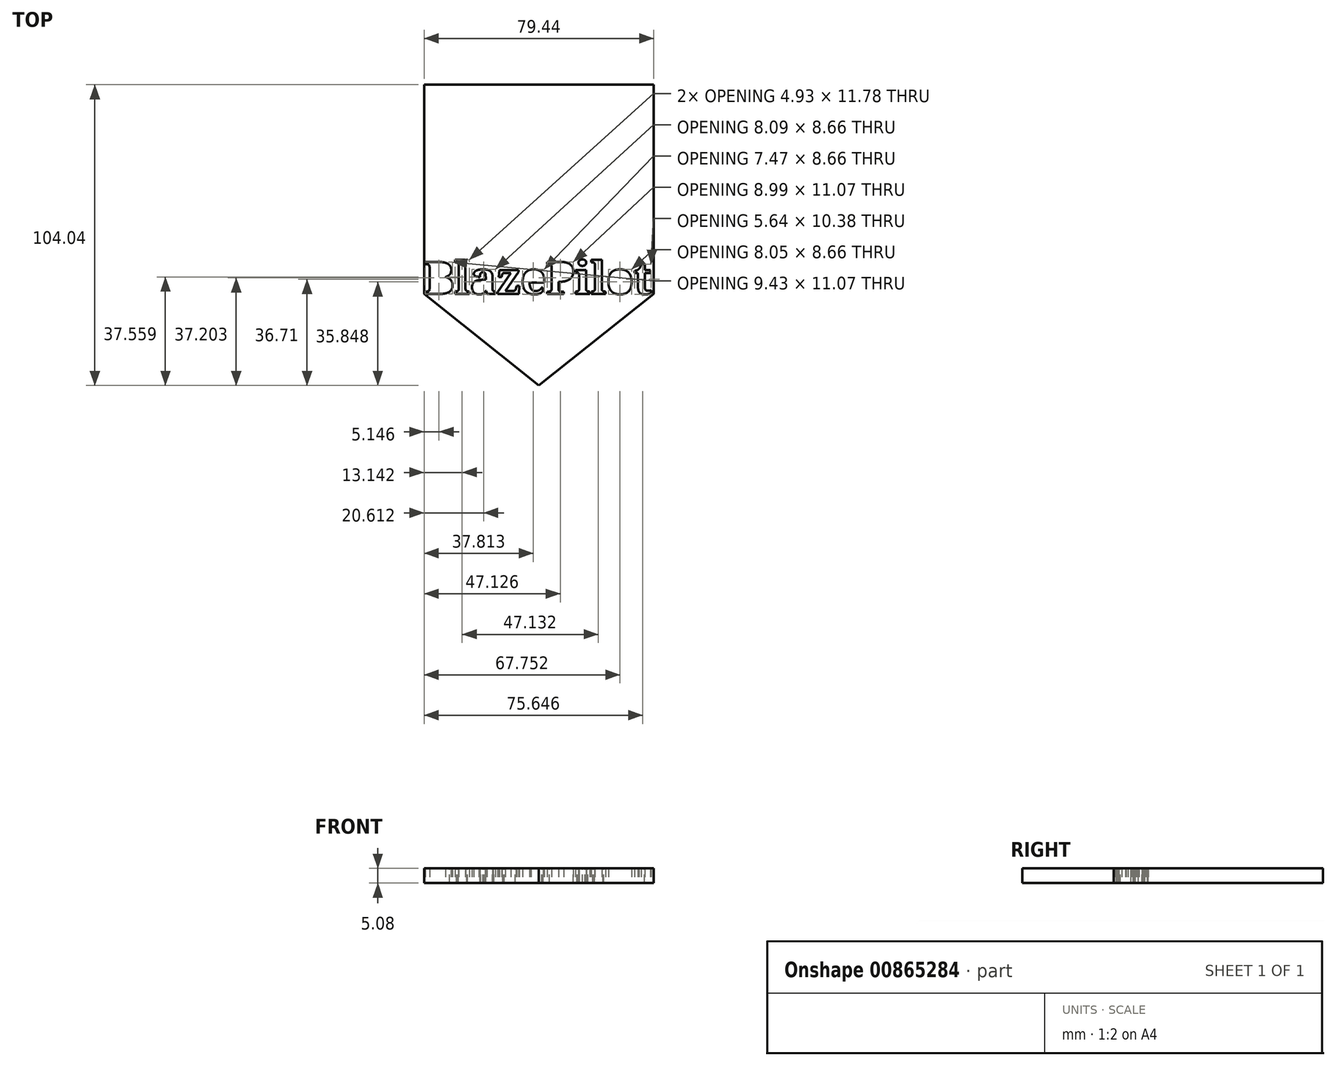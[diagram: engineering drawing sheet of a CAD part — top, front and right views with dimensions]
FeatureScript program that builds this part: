
annotation { "Feature Type Name" : "Feature", "Feature Type Description" : "" }
export const myFeature = defineFeature(function(context is Context, id is Id, definition is map)
    precondition{}
    {
        {
            var Q0;
            Q0=qCreatedBy(makeId("Top.planeOp"),FACE);
            var sketch = newSketch(context, id + "F0", { "sketchPlane" : qUnion([Q0])});
            skLineSegment(sketch, "E0", {"start": v(0, -55.27) * mm, "end": v(-39.72, -23.6) * mm});
            skLineSegment(sketch, "E1", {"start": v(0, -55.27) * mm, "end": v(39.72, -23.6) * mm});
            skLineSegment(sketch, "E2", {"start": v(-39.72, -23.6) * mm, "end": v(-39.72, 48.77) * mm});
            skLineSegment(sketch, "E3", {"start": v(39.72, -23.6) * mm, "end": v(39.72, 48.77) * mm});
            skLineSegment(sketch, "E4", {"start": v(-39.72, 48.77) * mm, "end": v(39.72, 48.77) * mm});
            skText(sketch, "E5", { "text": "BlazePilot", "fontName": "NotoSerif-Bold.ttf"});
            skLineSegment(sketch, "E6", {"start": v(-36.16, -10.08) * mm, "end": v(21.17, -10.08) * mm});
            const initialGuessF0  = {"E5": [-0.03972, -0.0236, 1, 0, 0.01116]};
            skSetInitialGuess(sketch, initialGuessF0);
            skSolve(sketch);
        }
        {
            var Q0;
            Q0 = qSketchRegion(id + "F0", true);
            extrude(context, id + "F1", {"entities" : qUnion([Q0]), "depth" : 2.54 * mm, "offsetDistance" : 25.4 * mm});
        }
        {
            var Q0;
            Q0 = qSketchRegion(id + "F0", true);
            var Q1;
            Q1=makeQuery(id+"F1.opExtrude","CAP_FACE",FACE,{"disambiguationData":[OSD([sQuery(id+"F0.wireOp",EDGE,"E0"),sQuery(id+"F0.wireOp",EDGE,"E1"),sQuery(id+"F0.wireOp",EDGE,"E2"),sQuery(id+"F0.wireOp",EDGE,"E3"),sQuery(id+"F0.wireOp",EDGE,"E4"),sQuery(id+"F0.wireOp",EDGE,"E5.sketch_text.stroke-0"),sQuery(id+"F0.wireOp",EDGE,"E5.sketch_text.stroke-1"),sQuery(id+"F0.wireOp",EDGE,"E5.sketch_text.stroke-2"),sQuery(id+"F0.wireOp",EDGE,"E5.sketch_text.stroke-3"),sQuery(id+"F0.wireOp",EDGE,"E5.sketch_text.stroke-4"),sQuery(id+"F0.wireOp",EDGE,"E5.sketch_text.stroke-5"),sQuery(id+"F0.wireOp",EDGE,"E5.sketch_text.stroke-6"),sQuery(id+"F0.wireOp",EDGE,"E5.sketch_text.stroke-7"),sQuery(id+"F0.wireOp",EDGE,"E5.sketch_text.stroke-8"),sQuery(id+"F0.wireOp",EDGE,"E5.sketch_text.stroke-9"),sQuery(id+"F0.wireOp",EDGE,"E5.sketch_text.stroke-10"),sQuery(id+"F0.wireOp",EDGE,"E5.sketch_text.stroke-11"),sQuery(id+"F0.wireOp",EDGE,"E5.sketch_text.stroke-12"),sQuery(id+"F0.wireOp",EDGE,"E5.sketch_text.stroke-13"),sQuery(id+"F0.wireOp",EDGE,"E5.sketch_text.stroke-14"),sQuery(id+"F0.wireOp",EDGE,"E5.sketch_text.stroke-15"),sQuery(id+"F0.wireOp",EDGE,"E5.sketch_text.stroke-16"),sQuery(id+"F0.wireOp",EDGE,"E5.sketch_text.stroke-17"),sQuery(id+"F0.wireOp",EDGE,"E5.sketch_text.stroke-18"),sQuery(id+"F0.wireOp",EDGE,"E5.sketch_text.stroke-19"),sQuery(id+"F0.wireOp",EDGE,"E5.sketch_text.stroke-20"),sQuery(id+"F0.wireOp",EDGE,"E5.sketch_text.stroke-21"),sQuery(id+"F0.wireOp",EDGE,"E5.sketch_text.stroke-22"),sQuery(id+"F0.wireOp",EDGE,"E5.sketch_text.stroke-23"),sQuery(id+"F0.wireOp",EDGE,"E5.sketch_text.stroke-24"),sQuery(id+"F0.wireOp",EDGE,"E5.sketch_text.stroke-25"),sQuery(id+"F0.wireOp",EDGE,"E5.sketch_text.stroke-26"),sQuery(id+"F0.wireOp",EDGE,"E5.sketch_text.stroke-27"),sQuery(id+"F0.wireOp",EDGE,"E5.sketch_text.stroke-50"),sQuery(id+"F0.wireOp",EDGE,"E5.sketch_text.stroke-51"),sQuery(id+"F0.wireOp",EDGE,"E5.sketch_text.stroke-52"),sQuery(id+"F0.wireOp",EDGE,"E5.sketch_text.stroke-53"),sQuery(id+"F0.wireOp",EDGE,"E5.sketch_text.stroke-54"),sQuery(id+"F0.wireOp",EDGE,"E5.sketch_text.stroke-55"),sQuery(id+"F0.wireOp",EDGE,"E5.sketch_text.stroke-56"),sQuery(id+"F0.wireOp",EDGE,"E5.sketch_text.stroke-57"),sQuery(id+"F0.wireOp",EDGE,"E5.sketch_text.stroke-58"),sQuery(id+"F0.wireOp",EDGE,"E5.sketch_text.stroke-59"),sQuery(id+"F0.wireOp",EDGE,"E5.sketch_text.stroke-60"),sQuery(id+"F0.wireOp",EDGE,"E5.sketch_text.stroke-61"),sQuery(id+"F0.wireOp",EDGE,"E5.sketch_text.stroke-62"),sQuery(id+"F0.wireOp",EDGE,"E5.sketch_text.stroke-63"),sQuery(id+"F0.wireOp",EDGE,"E5.sketch_text.stroke-64"),sQuery(id+"F0.wireOp",EDGE,"E5.sketch_text.stroke-65"),sQuery(id+"F0.wireOp",EDGE,"E5.sketch_text.stroke-66"),sQuery(id+"F0.wireOp",EDGE,"E5.sketch_text.stroke-67"),sQuery(id+"F0.wireOp",EDGE,"E5.sketch_text.stroke-68"),sQuery(id+"F0.wireOp",EDGE,"E5.sketch_text.stroke-69"),sQuery(id+"F0.wireOp",EDGE,"E5.sketch_text.stroke-70"),sQuery(id+"F0.wireOp",EDGE,"E5.sketch_text.stroke-71"),sQuery(id+"F0.wireOp",EDGE,"E5.sketch_text.stroke-84"),sQuery(id+"F0.wireOp",EDGE,"E5.sketch_text.stroke-85"),sQuery(id+"F0.wireOp",EDGE,"E5.sketch_text.stroke-86"),sQuery(id+"F0.wireOp",EDGE,"E5.sketch_text.stroke-87"),sQuery(id+"F0.wireOp",EDGE,"E5.sketch_text.stroke-88"),sQuery(id+"F0.wireOp",EDGE,"E5.sketch_text.stroke-89"),sQuery(id+"F0.wireOp",EDGE,"E5.sketch_text.stroke-90"),sQuery(id+"F0.wireOp",EDGE,"E5.sketch_text.stroke-91"),sQuery(id+"F0.wireOp",EDGE,"E5.sketch_text.stroke-92"),sQuery(id+"F0.wireOp",EDGE,"E5.sketch_text.stroke-93"),sQuery(id+"F0.wireOp",EDGE,"E5.sketch_text.stroke-94"),sQuery(id+"F0.wireOp",EDGE,"E5.sketch_text.stroke-95"),sQuery(id+"F0.wireOp",EDGE,"E5.sketch_text.stroke-96"),sQuery(id+"F0.wireOp",EDGE,"E5.sketch_text.stroke-97"),sQuery(id+"F0.wireOp",EDGE,"E5.sketch_text.stroke-98"),sQuery(id+"F0.wireOp",EDGE,"E5.sketch_text.stroke-99"),sQuery(id+"F0.wireOp",EDGE,"E5.sketch_text.stroke-100"),sQuery(id+"F0.wireOp",EDGE,"E5.sketch_text.stroke-101"),sQuery(id+"F0.wireOp",EDGE,"E5.sketch_text.stroke-102"),sQuery(id+"F0.wireOp",EDGE,"E5.sketch_text.stroke-103"),sQuery(id+"F0.wireOp",EDGE,"E5.sketch_text.stroke-104"),sQuery(id+"F0.wireOp",EDGE,"E5.sketch_text.stroke-105"),sQuery(id+"F0.wireOp",EDGE,"E5.sketch_text.stroke-106"),sQuery(id+"F0.wireOp",EDGE,"E5.sketch_text.stroke-107"),sQuery(id+"F0.wireOp",EDGE,"E5.sketch_text.stroke-108"),sQuery(id+"F0.wireOp",EDGE,"E5.sketch_text.stroke-109"),sQuery(id+"F0.wireOp",EDGE,"E5.sketch_text.stroke-110"),sQuery(id+"F0.wireOp",EDGE,"E5.sketch_text.stroke-111"),sQuery(id+"F0.wireOp",EDGE,"E5.sketch_text.stroke-112"),sQuery(id+"F0.wireOp",EDGE,"E5.sketch_text.stroke-113"),sQuery(id+"F0.wireOp",EDGE,"E5.sketch_text.stroke-114"),sQuery(id+"F0.wireOp",EDGE,"E5.sketch_text.stroke-115"),sQuery(id+"F0.wireOp",EDGE,"E5.sketch_text.stroke-116"),sQuery(id+"F0.wireOp",EDGE,"E5.sketch_text.stroke-117"),sQuery(id+"F0.wireOp",EDGE,"E5.sketch_text.stroke-118"),sQuery(id+"F0.wireOp",EDGE,"E5.sketch_text.stroke-119"),sQuery(id+"F0.wireOp",EDGE,"E5.sketch_text.stroke-120"),sQuery(id+"F0.wireOp",EDGE,"E5.sketch_text.stroke-121"),sQuery(id+"F0.wireOp",EDGE,"E5.sketch_text.stroke-122"),sQuery(id+"F0.wireOp",EDGE,"E5.sketch_text.stroke-123"),sQuery(id+"F0.wireOp",EDGE,"E5.sketch_text.stroke-124"),sQuery(id+"F0.wireOp",EDGE,"E5.sketch_text.stroke-125"),sQuery(id+"F0.wireOp",EDGE,"E5.sketch_text.stroke-126"),sQuery(id+"F0.wireOp",EDGE,"E5.sketch_text.stroke-127"),sQuery(id+"F0.wireOp",EDGE,"E5.sketch_text.stroke-128"),sQuery(id+"F0.wireOp",EDGE,"E5.sketch_text.stroke-129"),sQuery(id+"F0.wireOp",EDGE,"E5.sketch_text.stroke-130"),sQuery(id+"F0.wireOp",EDGE,"E5.sketch_text.stroke-131"),sQuery(id+"F0.wireOp",EDGE,"E5.sketch_text.stroke-132"),sQuery(id+"F0.wireOp",EDGE,"E5.sketch_text.stroke-133"),sQuery(id+"F0.wireOp",EDGE,"E5.sketch_text.stroke-134"),sQuery(id+"F0.wireOp",EDGE,"E5.sketch_text.stroke-135"),sQuery(id+"F0.wireOp",EDGE,"E5.sketch_text.stroke-136"),sQuery(id+"F0.wireOp",EDGE,"E5.sketch_text.stroke-137"),sQuery(id+"F0.wireOp",EDGE,"E5.sketch_text.stroke-138"),sQuery(id+"F0.wireOp",EDGE,"E5.sketch_text.stroke-139"),sQuery(id+"F0.wireOp",EDGE,"E5.sketch_text.stroke-140"),sQuery(id+"F0.wireOp",EDGE,"E5.sketch_text.stroke-141"),sQuery(id+"F0.wireOp",EDGE,"E5.sketch_text.stroke-142"),sQuery(id+"F0.wireOp",EDGE,"E5.sketch_text.stroke-143"),sQuery(id+"F0.wireOp",EDGE,"E5.sketch_text.stroke-144"),sQuery(id+"F0.wireOp",EDGE,"E5.sketch_text.stroke-145"),sQuery(id+"F0.wireOp",EDGE,"E5.sketch_text.stroke-153"),sQuery(id+"F0.wireOp",EDGE,"E5.sketch_text.stroke-154"),sQuery(id+"F0.wireOp",EDGE,"E5.sketch_text.stroke-155"),sQuery(id+"F0.wireOp",EDGE,"E5.sketch_text.stroke-156"),sQuery(id+"F0.wireOp",EDGE,"E5.sketch_text.stroke-157"),sQuery(id+"F0.wireOp",EDGE,"E5.sketch_text.stroke-158"),sQuery(id+"F0.wireOp",EDGE,"E5.sketch_text.stroke-159"),sQuery(id+"F0.wireOp",EDGE,"E5.sketch_text.stroke-160"),sQuery(id+"F0.wireOp",EDGE,"E5.sketch_text.stroke-161"),sQuery(id+"F0.wireOp",EDGE,"E5.sketch_text.stroke-162"),sQuery(id+"F0.wireOp",EDGE,"E5.sketch_text.stroke-163"),sQuery(id+"F0.wireOp",EDGE,"E5.sketch_text.stroke-164"),sQuery(id+"F0.wireOp",EDGE,"E5.sketch_text.stroke-165"),sQuery(id+"F0.wireOp",EDGE,"E5.sketch_text.stroke-166"),sQuery(id+"F0.wireOp",EDGE,"E5.sketch_text.stroke-167"),sQuery(id+"F0.wireOp",EDGE,"E5.sketch_text.stroke-168"),sQuery(id+"F0.wireOp",EDGE,"E5.sketch_text.stroke-169"),sQuery(id+"F0.wireOp",EDGE,"E5.sketch_text.stroke-170"),sQuery(id+"F0.wireOp",EDGE,"E5.sketch_text.stroke-171"),sQuery(id+"F0.wireOp",EDGE,"E5.sketch_text.stroke-172"),sQuery(id+"F0.wireOp",EDGE,"E5.sketch_text.stroke-173"),sQuery(id+"F0.wireOp",EDGE,"E5.sketch_text.stroke-174"),sQuery(id+"F0.wireOp",EDGE,"E5.sketch_text.stroke-175"),sQuery(id+"F0.wireOp",EDGE,"E5.sketch_text.stroke-176"),sQuery(id+"F0.wireOp",EDGE,"E5.sketch_text.stroke-177"),sQuery(id+"F0.wireOp",EDGE,"E5.sketch_text.stroke-178"),sQuery(id+"F0.wireOp",EDGE,"E5.sketch_text.stroke-179"),sQuery(id+"F0.wireOp",EDGE,"E5.sketch_text.stroke-180"),sQuery(id+"F0.wireOp",EDGE,"E5.sketch_text.stroke-181"),sQuery(id+"F0.wireOp",EDGE,"E5.sketch_text.stroke-182"),sQuery(id+"F0.wireOp",EDGE,"E5.sketch_text.stroke-183"),sQuery(id+"F0.wireOp",EDGE,"E5.sketch_text.stroke-184"),sQuery(id+"F0.wireOp",EDGE,"E5.sketch_text.stroke-185"),sQuery(id+"F0.wireOp",EDGE,"E5.sketch_text.stroke-186"),sQuery(id+"F0.wireOp",EDGE,"E5.sketch_text.stroke-187"),sQuery(id+"F0.wireOp",EDGE,"E5.sketch_text.stroke-188"),sQuery(id+"F0.wireOp",EDGE,"E5.sketch_text.stroke-189"),sQuery(id+"F0.wireOp",EDGE,"E5.sketch_text.stroke-190"),sQuery(id+"F0.wireOp",EDGE,"E5.sketch_text.stroke-191"),sQuery(id+"F0.wireOp",EDGE,"E5.sketch_text.stroke-192"),sQuery(id+"F0.wireOp",EDGE,"E5.sketch_text.stroke-193"),sQuery(id+"F0.wireOp",EDGE,"E5.sketch_text.stroke-194"),sQuery(id+"F0.wireOp",EDGE,"E5.sketch_text.stroke-195"),sQuery(id+"F0.wireOp",EDGE,"E5.sketch_text.stroke-196"),sQuery(id+"F0.wireOp",EDGE,"E5.sketch_text.stroke-197"),sQuery(id+"F0.wireOp",EDGE,"E5.sketch_text.stroke-198"),sQuery(id+"F0.wireOp",EDGE,"E5.sketch_text.stroke-199"),sQuery(id+"F0.wireOp",EDGE,"E5.sketch_text.stroke-200"),sQuery(id+"F0.wireOp",EDGE,"E5.sketch_text.stroke-201"),sQuery(id+"F0.wireOp",EDGE,"E5.sketch_text.stroke-202"),sQuery(id+"F0.wireOp",EDGE,"E5.sketch_text.stroke-203"),sQuery(id+"F0.wireOp",EDGE,"E5.sketch_text.stroke-204"),sQuery(id+"F0.wireOp",EDGE,"E5.sketch_text.stroke-205"),sQuery(id+"F0.wireOp",EDGE,"E5.sketch_text.stroke-206"),sQuery(id+"F0.wireOp",EDGE,"E5.sketch_text.stroke-207"),sQuery(id+"F0.wireOp",EDGE,"E5.sketch_text.stroke-208"),sQuery(id+"F0.wireOp",EDGE,"E5.sketch_text.stroke-209"),sQuery(id+"F0.wireOp",EDGE,"E5.sketch_text.stroke-210"),sQuery(id+"F0.wireOp",EDGE,"E5.sketch_text.stroke-222"),sQuery(id+"F0.wireOp",EDGE,"E5.sketch_text.stroke-223"),sQuery(id+"F0.wireOp",EDGE,"E5.sketch_text.stroke-224"),sQuery(id+"F0.wireOp",EDGE,"E5.sketch_text.stroke-225"),sQuery(id+"F0.wireOp",EDGE,"E5.sketch_text.stroke-226"),sQuery(id+"F0.wireOp",EDGE,"E5.sketch_text.stroke-227"),sQuery(id+"F0.wireOp",EDGE,"E5.sketch_text.stroke-228"),sQuery(id+"F0.wireOp",EDGE,"E5.sketch_text.stroke-229"),sQuery(id+"F0.wireOp",EDGE,"E5.sketch_text.stroke-230"),sQuery(id+"F0.wireOp",EDGE,"E5.sketch_text.stroke-231"),sQuery(id+"F0.wireOp",EDGE,"E5.sketch_text.stroke-232"),sQuery(id+"F0.wireOp",EDGE,"E5.sketch_text.stroke-233"),sQuery(id+"F0.wireOp",EDGE,"E5.sketch_text.stroke-234"),sQuery(id+"F0.wireOp",EDGE,"E5.sketch_text.stroke-235"),sQuery(id+"F0.wireOp",EDGE,"E5.sketch_text.stroke-236"),sQuery(id+"F0.wireOp",EDGE,"E5.sketch_text.stroke-237"),sQuery(id+"F0.wireOp",EDGE,"E5.sketch_text.stroke-238"),sQuery(id+"F0.wireOp",EDGE,"E5.sketch_text.stroke-239"),sQuery(id+"F0.wireOp",EDGE,"E5.sketch_text.stroke-240"),sQuery(id+"F0.wireOp",EDGE,"E5.sketch_text.stroke-241"),sQuery(id+"F0.wireOp",EDGE,"E5.sketch_text.stroke-242"),sQuery(id+"F0.wireOp",EDGE,"E5.sketch_text.stroke-243"),sQuery(id+"F0.wireOp",EDGE,"E5.sketch_text.stroke-244"),sQuery(id+"F0.wireOp",EDGE,"E5.sketch_text.stroke-245"),sQuery(id+"F0.wireOp",EDGE,"E5.sketch_text.stroke-246"),sQuery(id+"F0.wireOp",EDGE,"E5.sketch_text.stroke-247"),sQuery(id+"F0.wireOp",EDGE,"E5.sketch_text.stroke-248"),sQuery(id+"F0.wireOp",EDGE,"E5.sketch_text.stroke-249"),sQuery(id+"F0.wireOp",EDGE,"E5.sketch_text.stroke-250"),sQuery(id+"F0.wireOp",EDGE,"E5.sketch_text.stroke-251"),sQuery(id+"F0.wireOp",EDGE,"E5.sketch_text.stroke-252"),sQuery(id+"F0.wireOp",EDGE,"E5.sketch_text.stroke-253"),sQuery(id+"F0.wireOp",EDGE,"E5.sketch_text.stroke-254"),sQuery(id+"F0.wireOp",EDGE,"E5.sketch_text.stroke-255"),sQuery(id+"F0.wireOp",EDGE,"E5.sketch_text.stroke-256"),sQuery(id+"F0.wireOp",EDGE,"E5.sketch_text.stroke-257"),sQuery(id+"F0.wireOp",EDGE,"E5.sketch_text.stroke-258"),sQuery(id+"F0.wireOp",EDGE,"E5.sketch_text.stroke-259"),sQuery(id+"F0.wireOp",EDGE,"E5.sketch_text.stroke-260"),sQuery(id+"F0.wireOp",EDGE,"E5.sketch_text.stroke-261"),sQuery(id+"F0.wireOp",EDGE,"E5.sketch_text.stroke-262"),sQuery(id+"F0.wireOp",EDGE,"E5.sketch_text.stroke-263"),sQuery(id+"F0.wireOp",EDGE,"E5.sketch_text.stroke-264"),sQuery(id+"F0.wireOp",EDGE,"E5.sketch_text.stroke-265"),sQuery(id+"F0.wireOp",EDGE,"E5.sketch_text.stroke-266"),sQuery(id+"F0.wireOp",EDGE,"E5.sketch_text.stroke-267"),sQuery(id+"F0.wireOp",EDGE,"E5.sketch_text.stroke-268"),sQuery(id+"F0.wireOp",EDGE,"E5.sketch_text.stroke-269"),sQuery(id+"F0.wireOp",EDGE,"E5.sketch_text.stroke-270"),sQuery(id+"F0.wireOp",EDGE,"E5.sketch_text.stroke-271"),sQuery(id+"F0.wireOp",EDGE,"E5.sketch_text.stroke-272"),sQuery(id+"F0.wireOp",EDGE,"E5.sketch_text.stroke-273"),sQuery(id+"F0.wireOp",EDGE,"E5.sketch_text.stroke-274"),sQuery(id+"F0.wireOp",EDGE,"E5.sketch_text.stroke-275"),sQuery(id+"F0.wireOp",EDGE,"E5.sketch_text.stroke-276"),sQuery(id+"F0.wireOp",EDGE,"E5.sketch_text.stroke-277"),sQuery(id+"F0.wireOp",EDGE,"E5.sketch_text.stroke-278"),sQuery(id+"F0.wireOp",EDGE,"E5.sketch_text.stroke-279"),sQuery(id+"F0.wireOp",EDGE,"E5.sketch_text.stroke-280"),sQuery(id+"F0.wireOp",EDGE,"E5.sketch_text.stroke-281"),sQuery(id+"F0.wireOp",EDGE,"E5.sketch_text.stroke-282"),sQuery(id+"F0.wireOp",EDGE,"E5.sketch_text.stroke-283"),sQuery(id+"F0.wireOp",EDGE,"E5.sketch_text.stroke-284"),sQuery(id+"F0.wireOp",EDGE,"E5.sketch_text.stroke-285"),sQuery(id+"F0.wireOp",EDGE,"E5.sketch_text.stroke-286"),sQuery(id+"F0.wireOp",EDGE,"E5.sketch_text.stroke-287"),sQuery(id+"F0.wireOp",EDGE,"E5.sketch_text.stroke-288"),sQuery(id+"F0.wireOp",EDGE,"E5.sketch_text.stroke-289"),sQuery(id+"F0.wireOp",EDGE,"E5.sketch_text.stroke-290"),sQuery(id+"F0.wireOp",EDGE,"E5.sketch_text.stroke-291"),sQuery(id+"F0.wireOp",EDGE,"E5.sketch_text.stroke-292"),sQuery(id+"F0.wireOp",EDGE,"E5.sketch_text.stroke-293"),sQuery(id+"F0.wireOp",EDGE,"E5.sketch_text.stroke-310"),sQuery(id+"F0.wireOp",EDGE,"E5.sketch_text.stroke-311"),sQuery(id+"F0.wireOp",EDGE,"E5.sketch_text.stroke-312"),sQuery(id+"F0.wireOp",EDGE,"E5.sketch_text.stroke-313"),sQuery(id+"F0.wireOp",EDGE,"E5.sketch_text.stroke-314"),sQuery(id+"F0.wireOp",EDGE,"E5.sketch_text.stroke-315"),sQuery(id+"F0.wireOp",EDGE,"E5.sketch_text.stroke-316"),sQuery(id+"F0.wireOp",EDGE,"E5.sketch_text.stroke-317"),sQuery(id+"F0.wireOp",EDGE,"E5.sketch_text.stroke-318"),sQuery(id+"F0.wireOp",EDGE,"E5.sketch_text.stroke-319"),sQuery(id+"F0.wireOp",EDGE,"E5.sketch_text.stroke-320"),sQuery(id+"F0.wireOp",EDGE,"E5.sketch_text.stroke-321"),sQuery(id+"F0.wireOp",EDGE,"E5.sketch_text.stroke-322"),sQuery(id+"F0.wireOp",EDGE,"E5.sketch_text.stroke-323"),sQuery(id+"F0.wireOp",EDGE,"E5.sketch_text.stroke-324"),sQuery(id+"F0.wireOp",EDGE,"E5.sketch_text.stroke-325"),sQuery(id+"F0.wireOp",EDGE,"E5.sketch_text.stroke-326"),sQuery(id+"F0.wireOp",EDGE,"E5.sketch_text.stroke-327"),sQuery(id+"F0.wireOp",EDGE,"E5.sketch_text.stroke-328"),sQuery(id+"F0.wireOp",EDGE,"E5.sketch_text.stroke-329"),sQuery(id+"F0.wireOp",EDGE,"E5.sketch_text.stroke-330"),sQuery(id+"F0.wireOp",EDGE,"E5.sketch_text.stroke-331"),sQuery(id+"F0.wireOp",EDGE,"E5.sketch_text.stroke-332"),sQuery(id+"F0.wireOp",EDGE,"E5.sketch_text.stroke-333"),sQuery(id+"F0.wireOp",EDGE,"E5.sketch_text.stroke-334")])],"isStart":false});
            extrude(context, id + "F2", {"entities" : qUnion([Q0, Q1]), "operationType" : NewBodyOperationType.ADD, "depth" : 2.54 * mm, "offsetDistance" : 25.4 * mm});
        }
    });
